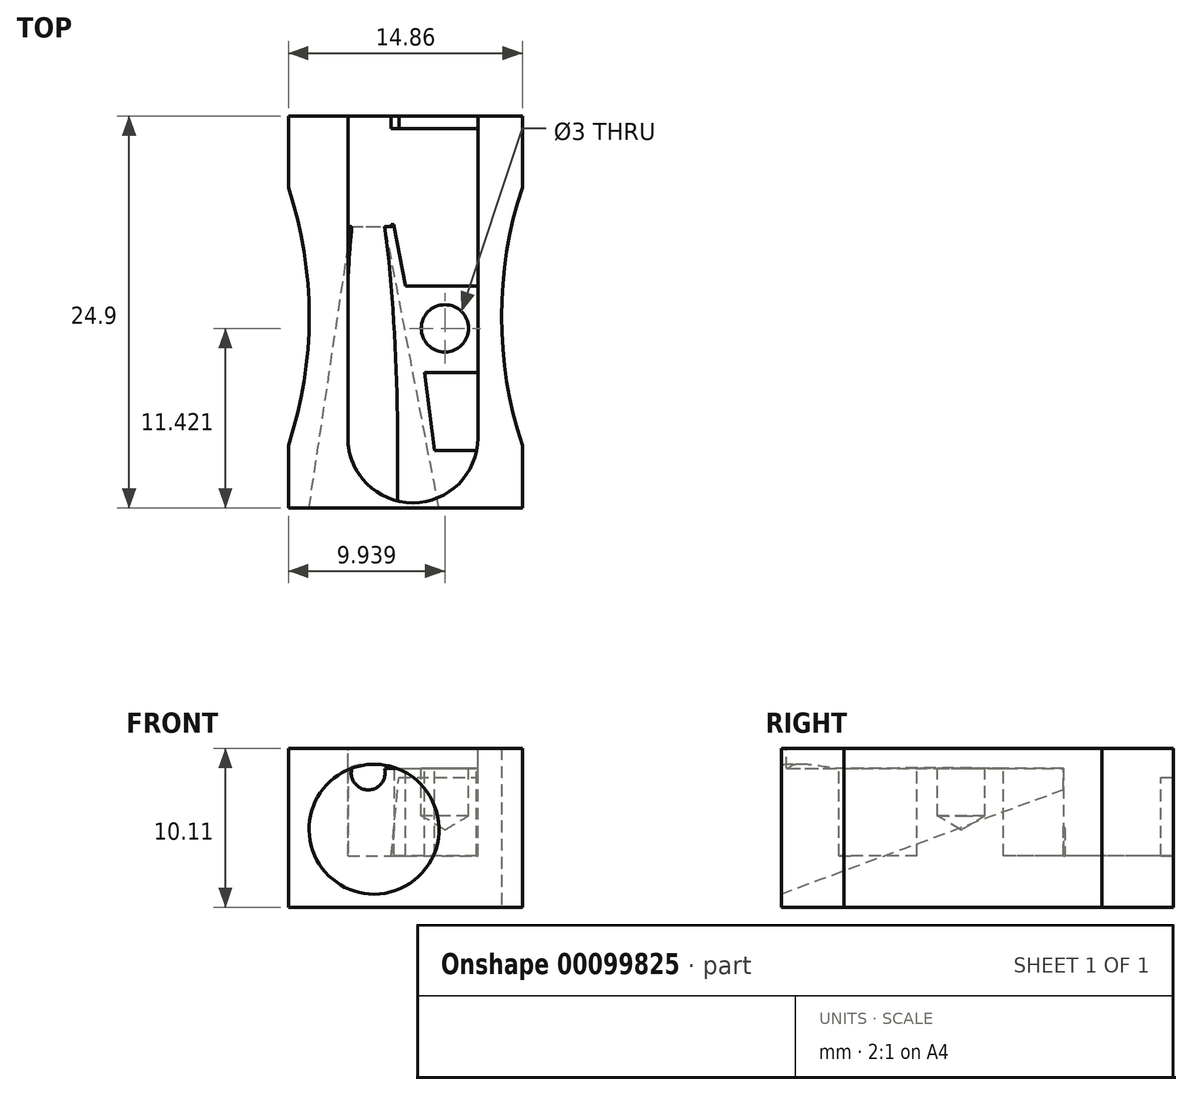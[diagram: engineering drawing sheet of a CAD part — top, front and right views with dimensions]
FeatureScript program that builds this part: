
annotation { "Feature Type Name" : "Feature", "Feature Type Description" : "" }
export const myFeature = defineFeature(function(context is Context, id is Id, definition is map)
    precondition{}
    {
        {
            var Q0;
            Q0=qCreatedBy(makeId("Top.planeOp"),FACE);
            var sketch = newSketch(context, id + "F0", { "sketchPlane" : qUnion([Q0])});
            skLineSegment(sketch, "E0.bottom", {"start": v(-7.43, 24.9) * mm, "end": v(7.43, 24.9) * mm});
            skLineSegment(sketch, "E0.top", {"start": v(-7.43, 0) * mm, "end": v(7.43, 0) * mm});
            skLineSegment(sketch, "E0.left", {"start": v(-7.43, 24.9) * mm, "end": v(-7.43, 20.36) * mm});
            skLineSegment(sketch, "E0.right", {"start": v(7.42, 24.9) * mm, "end": v(7.42, 20.36) * mm});
            skArc(sketch, "E1", {"start": v(-7.42, 3.99) * mm, "mid": v(-6.11, 12.18) * mm, "end": v(-7.43, 20.36) * mm});
            skArc(sketch, "E2.MirrorC", {"start": v(7.42, 3.99) * mm, "mid": v(6.11, 12.18) * mm, "end": v(7.43, 20.36) * mm});
            skLineSegment(sketch, "E3.trimOffspring", {"start": v(-7.43, 3.99) * mm, "end": v(-7.43, 0) * mm});
            skLineSegment(sketch, "E4.trimOffspring", {"start": v(7.43, 3.99) * mm, "end": v(7.43, 0) * mm});
            skSolve(sketch);
        }
        {
            var Q0;
            Q0 = qSketchRegion(id + "F0", true);
            extrude(context, id + "F1", {"entities" : qUnion([Q0]), "depth" : 10.1 * mm});
        }
        {
            var Q0;
            Q0=makeQuery(id+"F1.opExtrude","CAP_FACE",FACE,{"disambiguationData":[OSD([sQuery(id+"F0.wireOp",EDGE,"E0.bottom"),sQuery(id+"F0.wireOp",EDGE,"E0.top"),sQuery(id+"F0.wireOp",EDGE,"E0.left"),sQuery(id+"F0.wireOp",EDGE,"E0.right"),sQuery(id+"F0.wireOp",EDGE,"E1"),sQuery(id+"F0.wireOp",EDGE,"E2.MirrorC"),sQuery(id+"F0.wireOp",EDGE,"E3.trimOffspring"),sQuery(id+"F0.wireOp",EDGE,"E4.trimOffspring")])],"isStart":false});
            var sketch = newSketch(context, id + "F2", { "sketchPlane" : qUnion([Q0])});
            skLineSegment(sketch, "E5", {"start": v(-3.66, 24.9) * mm, "end": v(-3.66, 4.47) * mm});
            skLineSegment(sketch, "E6", {"start": v(4.6, 24.9) * mm, "end": v(4.6, 4.47) * mm});
            skArc(sketch, "E7", {"start": v(-3.66, 4.47) * mm, "mid": v(0.47, 0.34) * mm, "end": v(4.6, 4.47) * mm});
            skSolve(sketch);
        }
        {
            var Q0;
            {var subQ0=sQuery(id+"F2.wireOp",EDGE,"E5");Q0=makeQuery(id+"F2.imprint","IMPRINT",FACE,{"disambiguationData":[TD([[makeQuery(id+"F2.imprint","IMPRINT",EDGE,{"derivedFrom":subQ0}),1.0]])]});}
            extrude(context, id + "F3", {"entities" : qUnion([Q0]), "operationType" : NewBodyOperationType.REMOVE, "oppositeDirection" : true, "depth" : 1.29 * mm});
        }
        {
            var Q0;
            Q0=makeQuery(id+"F1.opExtrude","SWEPT_FACE",FACE,{"disambiguationData":[OSD([sQuery(id+"F0.wireOp",EDGE,"E0.top")])]});
            var sketch = newSketch(context, id + "F4", { "sketchPlane" : qUnion([Q0])});
            skCircle(sketch, "E8", {"center": v(-2, 4.97) * mm, "radius": 4.12 * mm});
            skSolve(sketch);
        }
        {
            var Q0;
            Q0=makeQuery(id+"F4.imprint","IMPRINT",FACE,{"disambiguationData":[TD([[makeQuery(id+"F4.imprint","IMPRINT",EDGE,{"derivedFrom":sQuery(id+"F4.wireOp",EDGE,"E8")}),-1.0]])]});
            cPlane(context, id + "F5", {"entities" : qUnion([Q0]), "cplaneType" : CPlaneType.OFFSET, "offset" : 18 * mm, "oppositeDirection" : true, "width" : 150 * mm, "height" : 150 * mm});
        }
        {
            var Q0;
            Q0=qCreatedBy(id+"F5.planeOp",FACE);
            var sketch = newSketch(context, id + "F6", { "sketchPlane" : qUnion([Q0])});
            skCircle(sketch, "E9", {"center": v(-2.37, 8.56) * mm, "radius": 1.06 * mm});
            skSolve(sketch);
        }
        {
            var Q1;
            Q1=makeQuery(id+"F4.imprint","IMPRINT",FACE,{"disambiguationData":[TD([[makeQuery(id+"F4.imprint","IMPRINT",EDGE,{"derivedFrom":sQuery(id+"F4.wireOp",EDGE,"E8")}),1.0]])]});
            var Q2;
            Q2=makeQuery(id+"F6.imprint","IMPRINT",FACE,{"disambiguationData":[TD([[makeQuery(id+"F6.imprint","IMPRINT",EDGE,{"derivedFrom":sQuery(id+"F6.wireOp",EDGE,"E9")}),1.0]])]});
            loft(context, id + "F7", {"operationType" : NewBodyOperationType.REMOVE, "sheetProfilesArray" : [{ "sheetProfileEntities" : qUnion([Q1]) }, { "sheetProfileEntities" : qUnion([Q2]) }]});
        }
        {
            var Q0;
            Q0=makeQuery(id+"F3.boolean.opBoolean","COPY",FACE,{"derivedFrom":makeQuery(id+"F3.opExtrude","CAP_FACE",FACE,{"disambiguationData":[OSD([sQuery(id+"F0.wireOp",EDGE,"E0.bottom"),sQuery(id+"F2.wireOp",EDGE,"E5"),sQuery(id+"F2.wireOp",EDGE,"E6"),sQuery(id+"F2.wireOp",EDGE,"E7")])],"isStart":false})});
            var sketch = newSketch(context, id + "F8", { "sketchPlane" : qUnion([Q0])});
            skLineSegment(sketch, "E10.bottom", {"start": v(4.6, 8.62) * mm, "end": v(1.23, 8.62) * mm});
            skLineSegment(sketch, "E10.top", {"start": v(4.6, 3.66) * mm, "end": v(1.87, 3.66) * mm});
            skLineSegment(sketch, "E10.left", {"start": v(4.6, 8.62) * mm, "end": v(4.6, 3.66) * mm});
            skLineSegment(sketch, "E10.right", {"start": v(1.23, 8.62) * mm, "end": v(1.87, 3.66) * mm});
            skLineSegment(sketch, "E11", {"start": v(0, 14.11) * mm, "end": v(4.6, 14.11) * mm});
            skPoint(sketch, "E11.endSnap0", {"position": v(4.6, 14.68) * mm});
            skLineSegment(sketch, "E12", {"start": v(4.6, 14.11) * mm, "end": v(4.6, 24.1) * mm});
            skLineSegment(sketch, "E13", {"start": v(4.6, 24.1) * mm, "end": v(-3.66, 24.1) * mm});
            skLineSegment(sketch, "E14", {"start": v(-3.66, 24.1) * mm, "end": v(-3.66, 18) * mm});
            skLineSegment(sketch, "E15", {"start": v(-3.66, 18) * mm, "end": v(-0.73, 18) * mm});
            skLineSegment(sketch, "E16", {"start": v(-0.73, 18) * mm, "end": v(0, 14.11) * mm});
            skSolve(sketch);
        }
        {
            var Q0;
            {var subQ8=sQuery(id+"F8.wireOp",EDGE,"E10.bottom");Q0=makeQuery(id+"F8.imprint","IMPRINT",FACE,{"disambiguationData":[TD([[makeQuery(id+"F8.imprint","IMPRINT",EDGE,{"derivedFrom":subQ8}),1.0]])]});}
            extrude(context, id + "F9", {"entities" : qUnion([Q0]), "operationType" : NewBodyOperationType.REMOVE, "oppositeDirection" : true, "depth" : 5.54 * mm});
        }
        {
            var Q0;
            Q0=makeQuery(id+"F8.imprint","IMPRINT",FACE,{"disambiguationData":[TD([[makeQuery(id+"F8.imprint","IMPRINT",EDGE,{"derivedFrom":sQuery(id+"F8.wireOp",EDGE,"E11")}),1.0]])]});
            extrude(context, id + "F10", {"entities" : qUnion([Q0]), "operationType" : NewBodyOperationType.REMOVE, "oppositeDirection" : true, "depth" : 5.54 * mm});
        }
        {
            var Q0;
            {var subQ0=sQuery(id+"F2.wireOp",EDGE,"E7");var subQ1=sQuery(id+"F2.wireOp",EDGE,"E6");Q0=makeQuery(id+"F10.boolean.opBoolean","SPLIT",FACE,{"disambiguationData":[TD([makeQuery(id+"F3.boolean.opBoolean","COPY",FACE,{"derivedFrom":makeQuery(id+"F3.opExtrude","SWEPT_FACE",FACE,{"disambiguationData":[OSD([subQ1])]})}),makeQuery(id+"F3.boolean.opBoolean","COPY",FACE,{"derivedFrom":makeQuery(id+"F3.opExtrude","SWEPT_FACE",FACE,{"disambiguationData":[OSD([subQ0])]})}),makeQuery(id+"F7.boolean.opBoolean","COPY",FACE,{"derivedFrom":makeQuery(id+"F7.opLoft","SWEPT_FACE",FACE,{"disambiguationData":[OSD([sQuery(id+"F4.wireOp",EDGE,"E8"),sQuery(id+"F6.wireOp",EDGE,"E9")])]})}),makeQuery(id+"F9.opExtrude","SWEPT_FACE",FACE,{"disambiguationData":[OSD([sQuery(id+"F8.wireOp",EDGE,"E10.left")])]}),makeQuery(id+"F9.opExtrude","SWEPT_FACE",FACE,{"disambiguationData":[OSD([subQ0])]}),makeQuery(id+"F9.boolean.opBoolean","COPY",FACE,{"derivedFrom":makeQuery(id+"F9.opExtrude","SWEPT_FACE",FACE,{"disambiguationData":[OSD([sQuery(id+"F8.wireOp",EDGE,"E10.bottom")])]})}),makeQuery(id+"F9.boolean.opBoolean","COPY",FACE,{"derivedFrom":makeQuery(id+"F9.opExtrude","SWEPT_FACE",FACE,{"disambiguationData":[OSD([sQuery(id+"F8.wireOp",EDGE,"E10.top")])]})}),makeQuery(id+"F9.boolean.opBoolean","COPY",FACE,{"derivedFrom":makeQuery(id+"F9.opExtrude","SWEPT_FACE",FACE,{"disambiguationData":[OSD([sQuery(id+"F8.wireOp",EDGE,"E10.right")])]})}),makeQuery(id+"F10.opExtrude","SWEPT_FACE",FACE,{"disambiguationData":[OSD([sQuery(id+"F8.wireOp",EDGE,"E11")])]}),makeQuery(id+"F10.opExtrude","SWEPT_FACE",FACE,{"disambiguationData":[OSD([sQuery(id+"F8.wireOp",EDGE,"E12")])]}),makeQuery(id+"F10.opExtrude","SWEPT_FACE",FACE,{"disambiguationData":[OSD([sQuery(id+"F8.wireOp",EDGE,"E15")])]}),makeQuery(id+"F10.opExtrude","SWEPT_FACE",FACE,{"disambiguationData":[OSD([sQuery(id+"F8.wireOp",EDGE,"E16")])]})])],"derivedFrom":makeQuery(id+"F3.boolean.opBoolean","COPY",FACE,{"derivedFrom":makeQuery(id+"F3.opExtrude","CAP_FACE",FACE,{"disambiguationData":[OSD([sQuery(id+"F0.wireOp",EDGE,"E0.bottom"),sQuery(id+"F2.wireOp",EDGE,"E5"),subQ1,subQ0])],"isStart":false})})});}
            var sketch = newSketch(context, id + "F11", { "sketchPlane" : qUnion([Q0])});
            skPoint(sketch, "E17", {"position": v(2.5, 11.42) * mm});
            skSolve(sketch);
        }
        {
            var Q0;
            Q0=sQuery(id+"F11.wireOp",VERTEX,"E17");
            var Q1;
            Q1=makeQuery(id+"F1.opExtrude","SWEPT_BODY",BODY,{"disambiguationData":[OSD([sQuery(id+"F0.wireOp",EDGE,"E0.bottom"),sQuery(id+"F0.wireOp",EDGE,"E0.top"),sQuery(id+"F0.wireOp",EDGE,"E0.left"),sQuery(id+"F0.wireOp",EDGE,"E0.right"),sQuery(id+"F0.wireOp",EDGE,"E1"),sQuery(id+"F0.wireOp",EDGE,"E2.MirrorC"),sQuery(id+"F0.wireOp",EDGE,"E3.trimOffspring"),sQuery(id+"F0.wireOp",EDGE,"E4.trimOffspring")])]});
            hole(context, id + "F12", {"style" : HoleStyle.C_BORE, "endStyle" : HoleEndStyle.BLIND, "holeDiameter" : 3 * mm, "cBoreDiameter" : 3 * mm, "cBoreDepth" : 3 * mm, "holeDepth" : 3 * mm, "startFromSketch" : true, "locations" : qUnion([Q0]), "scope" : qUnion([Q1])});
        }
        {
            var Q0;
            Q0=makeQuery(id+"F1.opExtrude","SWEPT_FACE",FACE,{"disambiguationData":[OSD([sQuery(id+"F0.wireOp",EDGE,"E0.bottom")])]});
            var sketch = newSketch(context, id + "F13", { "sketchPlane" : qUnion([Q0])});
            skLineSegment(sketch, "E18", {"start": v(3.66, 8.82) * mm, "end": v(3.66, 3.28) * mm});
            skLineSegment(sketch, "E19", {"start": v(3.66, 3.28) * mm, "end": v(0.9, 3.28) * mm});
            skLineSegment(sketch, "E20", {"start": v(0.9, 3.28) * mm, "end": v(0.42, 8.26) * mm});
            skLineSegment(sketch, "E21", {"start": v(0.42, 8.26) * mm, "end": v(-4.6, 8.26) * mm});
            skLineSegment(sketch, "E22", {"start": v(-4.6, 8.26) * mm, "end": v(-4.6, 8.82) * mm});
            skSolve(sketch);
        }
        {
            var Q0;
            Q0=makeQuery(id+"F13.imprint","IMPRINT",FACE,{"disambiguationData":[TD([[makeQuery(id+"F13.imprint","IMPRINT",EDGE,{"derivedFrom":sQuery(id+"F13.wireOp",EDGE,"E18")}),-1.0]])]});
            extrude(context, id + "F14", {"entities" : qUnion([Q0]), "operationType" : NewBodyOperationType.REMOVE, "oppositeDirection" : true, "depth" : 7 * mm});
        }
    });
